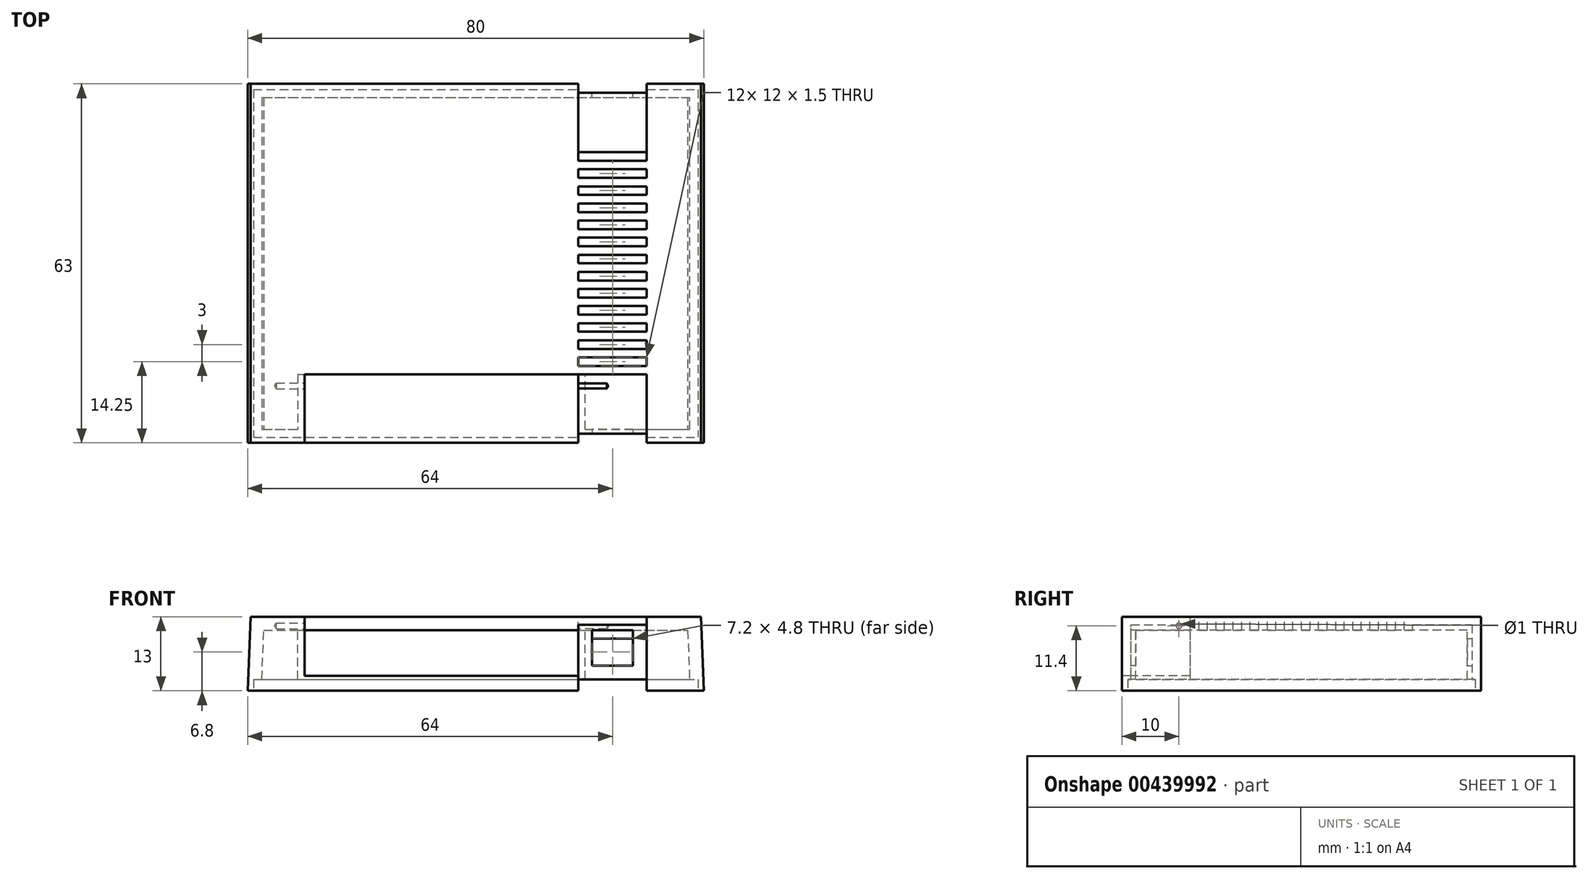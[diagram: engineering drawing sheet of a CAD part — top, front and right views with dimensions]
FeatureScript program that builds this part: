
annotation { "Feature Type Name" : "Feature", "Feature Type Description" : "" }
export const myFeature = defineFeature(function(context is Context, id is Id, definition is map)
    precondition{}
    {
        {
            var Q0;
            Q0=qCreatedBy(makeId("Top.planeOp"),FACE);
            var sketch = newSketch(context, id + "F0", { "sketchPlane" : qUnion([Q0])});
            skLineSegment(sketch, "E0.bottom", {"start": v(-40, 31.5) * mm, "end": v(40, 31.5) * mm});
            skLineSegment(sketch, "E0.top", {"start": v(-40, -31.5) * mm, "end": v(40, -31.5) * mm});
            skLineSegment(sketch, "E0.left", {"start": v(-40, 31.5) * mm, "end": v(-40, -31.5) * mm});
            skLineSegment(sketch, "E0.right", {"start": v(40, 31.5) * mm, "end": v(40, -31.5) * mm});
            skLineSegment(sketch, "E1.0", {"start": v(-39, -30.5) * mm, "end": v(39, -30.5) * mm});
            skLineSegment(sketch, "E1.1", {"start": v(-39, 30.5) * mm, "end": v(-39, -30.5) * mm});
            skLineSegment(sketch, "E1.2", {"start": v(-39, 30.5) * mm, "end": v(39, 30.5) * mm});
            skLineSegment(sketch, "E1.3", {"start": v(39, 30.5) * mm, "end": v(39, -30.5) * mm});
            skSolve(sketch);
        }
        {
            var Q0;
            Q0=qSketchRegion(id+"F0",true);
            var Q1;
            Q1=makeQuery(id+"F0.imprint","IMPRINT",FACE,{"disambiguationData":[TD([[makeQuery(id+"F0.imprint","IMPRINT",EDGE,{"derivedFrom":sQuery(id+"F0.wireOp",EDGE,"E0.bottom")}),-1.0]])]});
            var Q2;
            Q2=makeQuery(id+"F0.imprint","IMPRINT",FACE,{"disambiguationData":[TD([[makeQuery(id+"F0.imprint","IMPRINT",EDGE,{"derivedFrom":sQuery(id+"F0.wireOp",EDGE,"E1.0")}),1.0]])]});
            extrude(context, id + "F1", {"entities" : qUnion([Q0, Q1, Q2]), "depth" : 13 * mm});
        }
        {
            var Q0;
            Q0=makeQuery(id+"F1.opExtrude","SWEPT_FACE",FACE,{"disambiguationData":[OSD([sQuery(id+"F0.wireOp",EDGE,"E0.top")])]});
            var sketch = newSketch(context, id + "F2", { "sketchPlane" : qUnion([Q0])});
            skLineSegment(sketch, "E2.0", {"start": v(-40, 13) * mm, "end": v(-40, 0) * mm});
            skLineSegment(sketch, "E2.1", {"start": v(-40, 13) * mm, "end": v(40, 13) * mm});
            skLineSegment(sketch, "E2.2", {"start": v(40, 13) * mm, "end": v(40, 0) * mm});
            skLineSegment(sketch, "E2.3", {"start": v(-40, 0) * mm, "end": v(40, 0) * mm});
            skPoint(sketch, "E3", {"position": v(-39.5, 13) * mm});
            skPoint(sketch, "E4", {"position": v(39.5, 13) * mm});
            skLineSegment(sketch, "E5", {"start": v(-40, 0) * mm, "end": v(-39.5, 13) * mm});
            skLineSegment(sketch, "E6", {"start": v(39.5, 13) * mm, "end": v(40, 0) * mm});
            skPoint(sketch, "E7", {"position": v(30, 0) * mm});
            skPoint(sketch, "E8", {"position": v(18, 0) * mm});
            skPoint(sketch, "E9", {"position": v(30, 13) * mm});
            skPoint(sketch, "E10", {"position": v(18, 13) * mm});
            skLineSegment(sketch, "E11", {"start": v(18, 0) * mm, "end": v(18, 13) * mm});
            skLineSegment(sketch, "E12", {"start": v(30, 0) * mm, "end": v(30, 13) * mm});
            skPoint(sketch, "E13", {"position": v(-30, 0) * mm});
            skLineSegment(sketch, "E14", {"start": v(-30, 0) * mm, "end": v(-30, 13) * mm});
            skPoint(sketch, "E15", {"position": v(-30, 2.6) * mm});
            skLineSegment(sketch, "E16", {"start": v(-30, 2.6) * mm, "end": v(18, 2.6) * mm});
            skSolve(sketch);
        }
        {
            var Q0;
            {var subQ0=sQuery(id+"F2.wireOp",EDGE,"E2.0");Q0=makeQuery(id+"F2.imprint","IMPRINT",FACE,{"disambiguationData":[TD([[makeQuery(id+"F2.imprint","IMPRINT",EDGE,{"derivedFrom":subQ0}),1.0]])]});}
            var Q1;
            {var subQ0=sQuery(id+"F2.wireOp",EDGE,"E2.2");Q1=makeQuery(id+"F2.imprint","IMPRINT",FACE,{"disambiguationData":[TD([[makeQuery(id+"F2.imprint","IMPRINT",EDGE,{"derivedFrom":subQ0}),-1.0]])]});}
            extrude(context, id + "F3", {"entities" : qUnion([Q0, Q1]), "operationType" : NewBodyOperationType.REMOVE, "oppositeDirection" : true, "depth" : 63 * mm});
        }
        {
            var Q0;
            Q0=makeQuery(id+"F1.opExtrude","CAP_FACE",FACE,{"disambiguationData":[OSD([sQuery(id+"F0.wireOp",EDGE,"E0.bottom"),sQuery(id+"F0.wireOp",EDGE,"E0.top"),sQuery(id+"F0.wireOp",EDGE,"E0.left"),sQuery(id+"F0.wireOp",EDGE,"E0.right")])],"isStart":true});
            shell(context, id + "F4", {"entities" : qUnion([Q0]), "thickness" : 2.4 * mm});
        }
        {
            var Q0;
            Q0=makeQuery(id+"F0.imprint","IMPRINT",FACE,{"disambiguationData":[TD([[makeQuery(id+"F0.imprint","IMPRINT",EDGE,{"derivedFrom":sQuery(id+"F0.wireOp",EDGE,"E1.0")}),1.0]])]});
            extrude(context, id + "F5", {"entities" : qUnion([Q0]), "operationType" : NewBodyOperationType.REMOVE, "depth" : 2 * mm});
        }
        {
            var Q0;
            {var subQ0=sQuery(id+"F2.wireOp",EDGE,"E11");Q0=makeQuery(id+"F2.imprint","IMPRINT",FACE,{"disambiguationData":[TD([[makeQuery(id+"F2.imprint","IMPRINT",EDGE,{"derivedFrom":subQ0}),-1.0]])]});}
            extrude(context, id + "F6", {"entities" : qUnion([Q0]), "operationType" : NewBodyOperationType.REMOVE, "oppositeDirection" : true, "depth" : 1.6 * mm});
        }
        {
            var Q0;
            Q0=makeQuery(id+"F6.boolean.opBoolean","COPY",FACE,{"derivedFrom":makeQuery(id+"F6.opExtrude","CAP_FACE",FACE,{"disambiguationData":[OSD([sQuery(id+"F2.wireOp",EDGE,"E2.1"),sQuery(id+"F2.wireOp",EDGE,"E2.3"),sQuery(id+"F2.wireOp",EDGE,"E11"),sQuery(id+"F2.wireOp",EDGE,"E12")])],"isStart":false})});
            var sketch = newSketch(context, id + "F7", { "sketchPlane" : qUnion([Q0])});
            skLineSegment(sketch, "E17.0", {"start": v(20.4, 4.4) * mm, "end": v(20.4, 10.6) * mm});
            skLineSegment(sketch, "E17.1", {"start": v(20.4, 4.4) * mm, "end": v(27.6, 4.4) * mm});
            skLineSegment(sketch, "E17.2", {"start": v(27.6, 4.4) * mm, "end": v(27.6, 10.6) * mm});
            skLineSegment(sketch, "E17.3", {"start": v(20.4, 10.6) * mm, "end": v(27.6, 10.6) * mm});
            skLineSegment(sketch, "E18.0", {"start": v(-40, 0) * mm, "end": v(40, 0) * mm});
            skLineSegment(sketch, "E19.0", {"start": v(18, 13) * mm, "end": v(30, 13) * mm});
            skSolve(sketch);
        }
        {
            var Q0;
            Q0=makeQuery(id+"F7.imprint","IMPRINT",FACE,{"disambiguationData":[TD([[makeQuery(id+"F7.imprint","IMPRINT",EDGE,{"derivedFrom":sQuery(id+"F7.wireOp",EDGE,"E17.0")}),-1.0]])]});
            extrude(context, id + "F8", {"entities" : qUnion([Q0]), "operationType" : NewBodyOperationType.REMOVE, "oppositeDirection" : true, "depth" : 2 * mm});
        }
        {
            var Q0;
            Q0=makeQuery(id+"F1.opExtrude","CAP_FACE",FACE,{"disambiguationData":[OSD([sQuery(id+"F0.wireOp",EDGE,"E0.bottom"),sQuery(id+"F0.wireOp",EDGE,"E0.top"),sQuery(id+"F0.wireOp",EDGE,"E0.left"),sQuery(id+"F0.wireOp",EDGE,"E0.right")])],"isStart":false});
            var sketch = newSketch(context, id + "F9", { "sketchPlane" : qUnion([Q0])});
            skLineSegment(sketch, "E20.0", {"start": v(18, -29.9) * mm, "end": v(30, -29.9) * mm});
            skLineSegment(sketch, "E21", {"start": v(18, -29.9) * mm, "end": v(18, 31.5) * mm});
            skLineSegment(sketch, "E22", {"start": v(30, -29.9) * mm, "end": v(30, 31.5) * mm});
            skLineSegment(sketch, "E23.0", {"start": v(-40, -31.5) * mm, "end": v(40, -31.5) * mm});
            skLineSegment(sketch, "E24", {"start": v(18, -19.5) * mm, "end": v(30, -19.5) * mm});
            skLineSegment(sketch, "E25", {"start": v(18, 19.5) * mm, "end": v(30, 19.5) * mm});
            skLineSegment(sketch, "E26", {"start": v(18, 18) * mm, "end": v(30, 18) * mm});
            skLineSegment(sketch, "E27.0.1.0", {"start": v(18, 15) * mm, "end": v(30, 15) * mm});
            skLineSegment(sketch, "E27.0.1.1", {"start": v(18, 16.5) * mm, "end": v(30, 16.5) * mm});
            skLineSegment(sketch, "E27.0.2.0", {"start": v(18, 12) * mm, "end": v(30, 12) * mm});
            skLineSegment(sketch, "E27.0.2.1", {"start": v(18, 13.5) * mm, "end": v(30, 13.5) * mm});
            skLineSegment(sketch, "E27.0.3.0", {"start": v(18, 9) * mm, "end": v(30, 9) * mm});
            skLineSegment(sketch, "E27.0.3.1", {"start": v(18, 10.5) * mm, "end": v(30, 10.5) * mm});
            skLineSegment(sketch, "E27.0.4.0", {"start": v(18, 6) * mm, "end": v(30, 6) * mm});
            skLineSegment(sketch, "E27.0.4.1", {"start": v(18, 7.5) * mm, "end": v(30, 7.5) * mm});
            skLineSegment(sketch, "E27.0.5.0", {"start": v(18, 3) * mm, "end": v(30, 3) * mm});
            skLineSegment(sketch, "E27.0.5.1", {"start": v(18, 4.5) * mm, "end": v(30, 4.5) * mm});
            skLineSegment(sketch, "E27.0.6.0", {"start": v(18, 0) * mm, "end": v(30, 0) * mm});
            skLineSegment(sketch, "E27.0.6.1", {"start": v(18, 1.5) * mm, "end": v(30, 1.5) * mm});
            skLineSegment(sketch, "E27.0.7.0", {"start": v(18, -3) * mm, "end": v(30, -3) * mm});
            skLineSegment(sketch, "E27.0.7.1", {"start": v(18, -1.5) * mm, "end": v(30, -1.5) * mm});
            skLineSegment(sketch, "E27.0.8.0", {"start": v(18, -6) * mm, "end": v(30, -6) * mm});
            skLineSegment(sketch, "E27.0.8.1", {"start": v(18, -4.5) * mm, "end": v(30, -4.5) * mm});
            skLineSegment(sketch, "E27.0.9.0", {"start": v(18, -9) * mm, "end": v(30, -9) * mm});
            skLineSegment(sketch, "E27.0.9.1", {"start": v(18, -7.5) * mm, "end": v(30, -7.5) * mm});
            skLineSegment(sketch, "E27.0.10.0", {"start": v(18, -12) * mm, "end": v(30, -12) * mm});
            skLineSegment(sketch, "E27.0.10.1", {"start": v(18, -10.5) * mm, "end": v(30, -10.5) * mm});
            skLineSegment(sketch, "E27.0.11.0", {"start": v(18, -15) * mm, "end": v(30, -15) * mm});
            skLineSegment(sketch, "E27.0.11.1", {"start": v(18, -13.5) * mm, "end": v(30, -13.5) * mm});
            skLineSegment(sketch, "E27.0.12.0", {"start": v(18, -18) * mm, "end": v(30, -18) * mm});
            skLineSegment(sketch, "E27.0.12.1", {"start": v(18, -16.5) * mm, "end": v(30, -16.5) * mm});
            skLineSegment(sketch, "E27.direction1", {"start": v(18, 18) * mm, "end": v(39.8, 18) * mm, "construction": true});
            skLineSegment(sketch, "E27.direction2", {"start": v(18, 18) * mm, "end": v(18, 15) * mm, "construction": true});
            skSolve(sketch);
        }
        {
            var Q0;
            {var subQ3=sQuery(id+"F9.wireOp",EDGE,"E25");Q0=makeQuery(id+"F9.imprint","IMPRINT",FACE,{"disambiguationData":[TD([[makeQuery(id+"F9.imprint","IMPRINT",EDGE,{"derivedFrom":subQ3}),1.0]])]});}
            var Q1;
            {var subQ0=sQuery(id+"F9.wireOp",EDGE,"E20.0");Q1=makeQuery(id+"F9.imprint","IMPRINT",FACE,{"disambiguationData":[TD([[makeQuery(id+"F9.imprint","IMPRINT",EDGE,{"derivedFrom":subQ0}),1.0]])]});}
            extrude(context, id + "F10", {"entities" : qUnion([Q0, Q1]), "operationType" : NewBodyOperationType.REMOVE, "oppositeDirection" : true, "depth" : 1.4 * mm});
        }
        {
            var Q0;
            {var subQ0=sQuery(id+"F9.wireOp",EDGE,"E27.0.12.0");Q0=makeQuery(id+"F9.imprint","IMPRINT",FACE,{"disambiguationData":[TD([[makeQuery(id+"F9.imprint","IMPRINT",EDGE,{"derivedFrom":subQ0}),1.0]])]});}
            var Q1;
            {var subQ0=sQuery(id+"F9.wireOp",EDGE,"E27.0.11.0");Q1=makeQuery(id+"F9.imprint","IMPRINT",FACE,{"disambiguationData":[TD([[makeQuery(id+"F9.imprint","IMPRINT",EDGE,{"derivedFrom":subQ0}),1.0]])]});}
            var Q2;
            {var subQ0=sQuery(id+"F9.wireOp",EDGE,"E27.0.10.0");Q2=makeQuery(id+"F9.imprint","IMPRINT",FACE,{"disambiguationData":[TD([[makeQuery(id+"F9.imprint","IMPRINT",EDGE,{"derivedFrom":subQ0}),1.0]])]});}
            var Q3;
            {var subQ0=sQuery(id+"F9.wireOp",EDGE,"E27.0.9.0");Q3=makeQuery(id+"F9.imprint","IMPRINT",FACE,{"disambiguationData":[TD([[makeQuery(id+"F9.imprint","IMPRINT",EDGE,{"derivedFrom":subQ0}),1.0]])]});}
            var Q4;
            {var subQ0=sQuery(id+"F9.wireOp",EDGE,"E27.0.8.0");Q4=makeQuery(id+"F9.imprint","IMPRINT",FACE,{"disambiguationData":[TD([[makeQuery(id+"F9.imprint","IMPRINT",EDGE,{"derivedFrom":subQ0}),1.0]])]});}
            var Q5;
            {var subQ0=sQuery(id+"F9.wireOp",EDGE,"E27.0.6.0");Q5=makeQuery(id+"F9.imprint","IMPRINT",FACE,{"disambiguationData":[TD([[makeQuery(id+"F9.imprint","IMPRINT",EDGE,{"derivedFrom":subQ0}),1.0]])]});}
            var Q6;
            {var subQ0=sQuery(id+"F9.wireOp",EDGE,"E27.0.7.0");Q6=makeQuery(id+"F9.imprint","IMPRINT",FACE,{"disambiguationData":[TD([[makeQuery(id+"F9.imprint","IMPRINT",EDGE,{"derivedFrom":subQ0}),1.0]])]});}
            var Q7;
            {var subQ0=sQuery(id+"F9.wireOp",EDGE,"E27.0.5.0");Q7=makeQuery(id+"F9.imprint","IMPRINT",FACE,{"disambiguationData":[TD([[makeQuery(id+"F9.imprint","IMPRINT",EDGE,{"derivedFrom":subQ0}),1.0]])]});}
            var Q8;
            {var subQ0=sQuery(id+"F9.wireOp",EDGE,"E27.0.4.0");Q8=makeQuery(id+"F9.imprint","IMPRINT",FACE,{"disambiguationData":[TD([[makeQuery(id+"F9.imprint","IMPRINT",EDGE,{"derivedFrom":subQ0}),1.0]])]});}
            var Q9;
            {var subQ0=sQuery(id+"F9.wireOp",EDGE,"E27.0.3.0");Q9=makeQuery(id+"F9.imprint","IMPRINT",FACE,{"disambiguationData":[TD([[makeQuery(id+"F9.imprint","IMPRINT",EDGE,{"derivedFrom":subQ0}),1.0]])]});}
            var Q10;
            {var subQ0=sQuery(id+"F9.wireOp",EDGE,"E27.0.2.0");Q10=makeQuery(id+"F9.imprint","IMPRINT",FACE,{"disambiguationData":[TD([[makeQuery(id+"F9.imprint","IMPRINT",EDGE,{"derivedFrom":subQ0}),1.0]])]});}
            var Q11;
            {var subQ0=sQuery(id+"F9.wireOp",EDGE,"E27.0.1.0");Q11=makeQuery(id+"F9.imprint","IMPRINT",FACE,{"disambiguationData":[TD([[makeQuery(id+"F9.imprint","IMPRINT",EDGE,{"derivedFrom":subQ0}),1.0]])]});}
            var Q12;
            {var subQ0=sQuery(id+"F9.wireOp",EDGE,"E25");Q12=makeQuery(id+"F9.imprint","IMPRINT",FACE,{"disambiguationData":[TD([[makeQuery(id+"F9.imprint","IMPRINT",EDGE,{"derivedFrom":subQ0}),-1.0]])]});}
            extrude(context, id + "F11", {"entities" : qUnion([Q0, Q1, Q2, Q3, Q4, Q5, Q6, Q7, Q8, Q9, Q10, Q11, Q12]), "operationType" : NewBodyOperationType.REMOVE, "oppositeDirection" : true, "depth" : 3 * mm});
        }
        {
            var Q0;
            Q0=makeQuery(id+"F1.opExtrude","SWEPT_FACE",FACE,{"disambiguationData":[OSD([sQuery(id+"F0.wireOp",EDGE,"E0.bottom")])]});
            var sketch = newSketch(context, id + "F12", { "sketchPlane" : qUnion([Q0])});
            skLineSegment(sketch, "E28.0", {"start": v(-18, 11.6) * mm, "end": v(-30, 11.6) * mm});
            skLineSegment(sketch, "E28.1", {"start": v(39, 0) * mm, "end": v(-39, 0) * mm});
            skLineSegment(sketch, "E29", {"start": v(-30, 11.6) * mm, "end": v(-30, 0) * mm});
            skLineSegment(sketch, "E30", {"start": v(-18, 11.6) * mm, "end": v(-18, 0) * mm});
            skSolve(sketch);
        }
        {
            var Q0;
            Q0=makeQuery(id+"F12.imprint","IMPRINT",FACE,{"disambiguationData":[TD([[makeQuery(id+"F12.imprint","IMPRINT",EDGE,{"derivedFrom":sQuery(id+"F12.wireOp",EDGE,"E28.0")}),1.0]])]});
            extrude(context, id + "F13", {"entities" : qUnion([Q0]), "operationType" : NewBodyOperationType.REMOVE, "oppositeDirection" : true, "depth" : 1.6 * mm});
        }
        {
            var Q0;
            Q0=makeQuery(id+"F13.boolean.opBoolean","COPY",FACE,{"derivedFrom":makeQuery(id+"F13.opExtrude","CAP_FACE",FACE,{"disambiguationData":[OSD([sQuery(id+"F12.wireOp",EDGE,"E28.0"),sQuery(id+"F12.wireOp",EDGE,"E28.1"),sQuery(id+"F12.wireOp",EDGE,"E29"),sQuery(id+"F12.wireOp",EDGE,"E30")])],"isStart":false})});
            var sketch = newSketch(context, id + "F14", { "sketchPlane" : qUnion([Q0])});
            skLineSegment(sketch, "E31.0", {"start": v(-20.4, 9.2) * mm, "end": v(-27.6, 9.2) * mm});
            skLineSegment(sketch, "E31.1", {"start": v(-20.4, 9.2) * mm, "end": v(-20.4, 4.4) * mm});
            skLineSegment(sketch, "E31.2", {"start": v(-27.6, 4.4) * mm, "end": v(-20.4, 4.4) * mm});
            skLineSegment(sketch, "E31.3", {"start": v(-27.6, 9.2) * mm, "end": v(-27.6, 4.4) * mm});
            skLineSegment(sketch, "E32.0", {"start": v(40, 0) * mm, "end": v(-40, 0) * mm});
            skLineSegment(sketch, "E33.0", {"start": v(-30, 13) * mm, "end": v(-39.5, 13) * mm});
            skSolve(sketch);
        }
        {
            var Q0;
            Q0=makeQuery(id+"F14.imprint","IMPRINT",FACE,{"disambiguationData":[TD([[makeQuery(id+"F14.imprint","IMPRINT",EDGE,{"derivedFrom":sQuery(id+"F14.wireOp",EDGE,"E31.0")}),1.0]])]});
            extrude(context, id + "F15", {"entities" : qUnion([Q0]), "operationType" : NewBodyOperationType.REMOVE, "oppositeDirection" : true, "depth" : 3 * mm});
        }
        {
            var Q0;
            {var subQ5=sQuery(id+"F2.wireOp",EDGE,"E16");Q0=makeQuery(id+"F2.imprint","IMPRINT",FACE,{"disambiguationData":[TD([[makeQuery(id+"F2.imprint","IMPRINT",EDGE,{"derivedFrom":subQ5}),1.0]])]});}
            extrude(context, id + "F16", {"entities" : qUnion([Q0]), "operationType" : NewBodyOperationType.REMOVE, "oppositeDirection" : true, "depth" : 12 * mm});
        }
        {
            var Q0;
            Q0=makeQuery(id+"F8.boolean.opBoolean","MERGE",FACE,{"derivedFrom":[makeQuery(id+"F4.opShell","OFFSET_FACE",FACE,{"disambiguationData":[OSD([sQuery(id+"F0.wireOp",EDGE,"E0.bottom"),sQuery(id+"F0.wireOp",EDGE,"E0.top"),sQuery(id+"F0.wireOp",EDGE,"E0.left"),sQuery(id+"F0.wireOp",EDGE,"E0.right")])]}),makeQuery(id+"F8.opExtrude","SWEPT_FACE",FACE,{"disambiguationData":[OSD([sQuery(id+"F7.wireOp",EDGE,"E17.3")])]})]});
            var sketch = newSketch(context, id + "F17", { "sketchPlane" : qUnion([Q0])});
            skLineSegment(sketch, "E34.0", {"start": v(-37.2, 29.1) * mm, "end": v(-30, 29.1) * mm});
            skLineSegment(sketch, "E34.1", {"start": v(-30, 29.1) * mm, "end": v(-30, 19.5) * mm});
            skLineSegment(sketch, "E34.2", {"start": v(-30, 19.5) * mm, "end": v(18, 19.5) * mm});
            skLineSegment(sketch, "E34.3", {"start": v(18, 29.1) * mm, "end": v(18, 19.5) * mm});
            skLineSegment(sketch, "E34.4", {"start": v(18, 29.1) * mm, "end": v(20.4, 29.1) * mm});
            skPoint(sketch, "E35", {"position": v(-31.2, 29.1) * mm});
            skPoint(sketch, "E36", {"position": v(-31.2, 19.5) * mm});
            skLineSegment(sketch, "E37", {"start": v(-31.2, 19.5) * mm, "end": v(-31.2, 29.1) * mm});
            skLineSegment(sketch, "E38", {"start": v(19.2, 29.1) * mm, "end": v(19.2, 18) * mm});
            skLineSegment(sketch, "E39", {"start": v(-31.2, 19.5) * mm, "end": v(-30, 19.5) * mm});
            skLineSegment(sketch, "E40", {"start": v(18, 19.5) * mm, "end": v(19.2, 19.5) * mm});
            skSolve(sketch);
        }
        {
            var Q0;
            {var subQ0=sQuery(id+"F17.wireOp",EDGE,"E34.3");Q0=makeQuery(id+"F17.imprint","IMPRINT",FACE,{"disambiguationData":[TD([[makeQuery(id+"F17.imprint","IMPRINT",EDGE,{"derivedFrom":subQ0}),1.0]])]});}
            var Q1;
            {var subQ0=sQuery(id+"F17.wireOp",EDGE,"E34.1");Q1=makeQuery(id+"F17.imprint","IMPRINT",FACE,{"disambiguationData":[TD([[makeQuery(id+"F17.imprint","IMPRINT",EDGE,{"derivedFrom":subQ0}),-1.0]])]});}
            extrude(context, id + "F18", {"entities" : qUnion([Q0, Q1]), "operationType" : NewBodyOperationType.ADD, "depth" : 8.6 * mm});
        }
        {
            var Q0;
            Q0=makeQuery(id+"F18.boolean.opBoolean","MERGE",FACE,{"derivedFrom":[makeQuery(id+"F16.boolean.opBoolean","COPY",FACE,{"derivedFrom":makeQuery(id+"F16.opExtrude","SWEPT_FACE",FACE,{"disambiguationData":[OSD([sQuery(id+"F2.wireOp",EDGE,"E14")])]})}),makeQuery(id+"F18.opExtrude","SWEPT_FACE",FACE,{"disambiguationData":[OSD([sQuery(id+"F17.wireOp",EDGE,"E34.1")])]})]});
            var sketch = newSketch(context, id + "F19", { "sketchPlane" : qUnion([Q0])});
            skPoint(sketch, "E41.0", {"position": v(-29.1, 2.6) * mm});
            skLineSegment(sketch, "E41.1", {"start": v(-29.1, 2) * mm, "end": v(-19.5, 2) * mm});
            skLineSegment(sketch, "E42.0", {"start": v(-19.5, 2) * mm, "end": v(-19.5, 10.6) * mm});
            skLineSegment(sketch, "E43", {"start": v(-29.1, 2.6) * mm, "end": v(-19.5, 2.6) * mm});
            skPoint(sketch, "E44", {"position": v(-21.5, 11.4) * mm});
            skLineSegment(sketch, "E45.0", {"start": v(-19.5, 10.6) * mm, "end": v(-19.5, 13) * mm});
            skLineSegment(sketch, "E46.0", {"start": v(-19.5, 13) * mm, "end": v(-31.5, 13) * mm});
            skLineSegment(sketch, "E47.0", {"start": v(-31.5, 2.6) * mm, "end": v(-31.5, 13) * mm});
            skSolve(sketch);
        }
        {
            var Q0;
            {var subQ0=sQuery(id+"F19.wireOp",EDGE,"E41.1");Q0=makeQuery(id+"F19.imprint","IMPRINT",FACE,{"disambiguationData":[TD([[makeQuery(id+"F19.imprint","IMPRINT",EDGE,{"derivedFrom":subQ0}),1.0]])]});}
            extrude(context, id + "F20", {"entities" : qUnion([Q0]), "operationType" : NewBodyOperationType.ADD, "depth" : 48 * mm});
        }
        {
            var Q0;
            Q0=sQuery(id+"F19.wireOp",VERTEX,"E44");
            var Q1;
            Q1=makeQuery(id+"F1.opExtrude","SWEPT_BODY",BODY,{"disambiguationData":[OSD([sQuery(id+"F0.wireOp",EDGE,"E0.bottom"),sQuery(id+"F0.wireOp",EDGE,"E0.top"),sQuery(id+"F0.wireOp",EDGE,"E0.left"),sQuery(id+"F0.wireOp",EDGE,"E0.right")])]});
            hole(context, id + "F21", {"style" : HoleStyle.SIMPLE, "endStyle" : HoleEndStyle.BLIND, "holeDiameter" : 1 * mm, "holeDepth" : 5 * mm, "isTappedThrough" : true, "tappedDepth" : 12 * mm, "tapClearance" : 3, "startFromSketch" : true, "locations" : qUnion([Q0]), "scope" : qUnion([Q1])});
        }
        {
            var Q0;
            Q0=makeQuery(id+"F18.boolean.opBoolean","MERGE",FACE,{"derivedFrom":[makeQuery(id+"F16.boolean.opBoolean","COPY",FACE,{"derivedFrom":makeQuery(id+"F16.opExtrude","SWEPT_FACE",FACE,{"disambiguationData":[OSD([sQuery(id+"F2.wireOp",EDGE,"E11")])]})}),makeQuery(id+"F18.opExtrude","SWEPT_FACE",FACE,{"disambiguationData":[OSD([sQuery(id+"F17.wireOp",EDGE,"E34.3")])]})]});
            var sketch = newSketch(context, id + "F22", { "sketchPlane" : qUnion([Q0])});
            skLineSegment(sketch, "E48.0", {"start": v(29.9, 11.6) * mm, "end": v(19.5, 11.6) * mm});
            skLineSegment(sketch, "E48.1", {"start": v(19.5, 2.6) * mm, "end": v(19.5, 10.6) * mm});
            skLineSegment(sketch, "E48.2", {"start": v(19.5, 2.6) * mm, "end": v(29.9, 2.6) * mm});
            skPoint(sketch, "E49", {"position": v(21.5, 11.4) * mm});
            skSolve(sketch);
        }
        {
            var Q0;
            Q0=sQuery(id+"F22.wireOp",VERTEX,"E49");
            var Q1;
            Q1=makeQuery(id+"F1.opExtrude","SWEPT_BODY",BODY,{"disambiguationData":[OSD([sQuery(id+"F0.wireOp",EDGE,"E0.bottom"),sQuery(id+"F0.wireOp",EDGE,"E0.top"),sQuery(id+"F0.wireOp",EDGE,"E0.left"),sQuery(id+"F0.wireOp",EDGE,"E0.right")])]});
            hole(context, id + "F23", {"style" : HoleStyle.SIMPLE, "endStyle" : HoleEndStyle.BLIND, "holeDiameter" : 1 * mm, "holeDepth" : 5 * mm, "isTappedThrough" : true, "tappedDepth" : 12 * mm, "tapClearance" : 3, "startFromSketch" : true, "locations" : qUnion([Q0]), "scope" : qUnion([Q1])});
        }
    });
